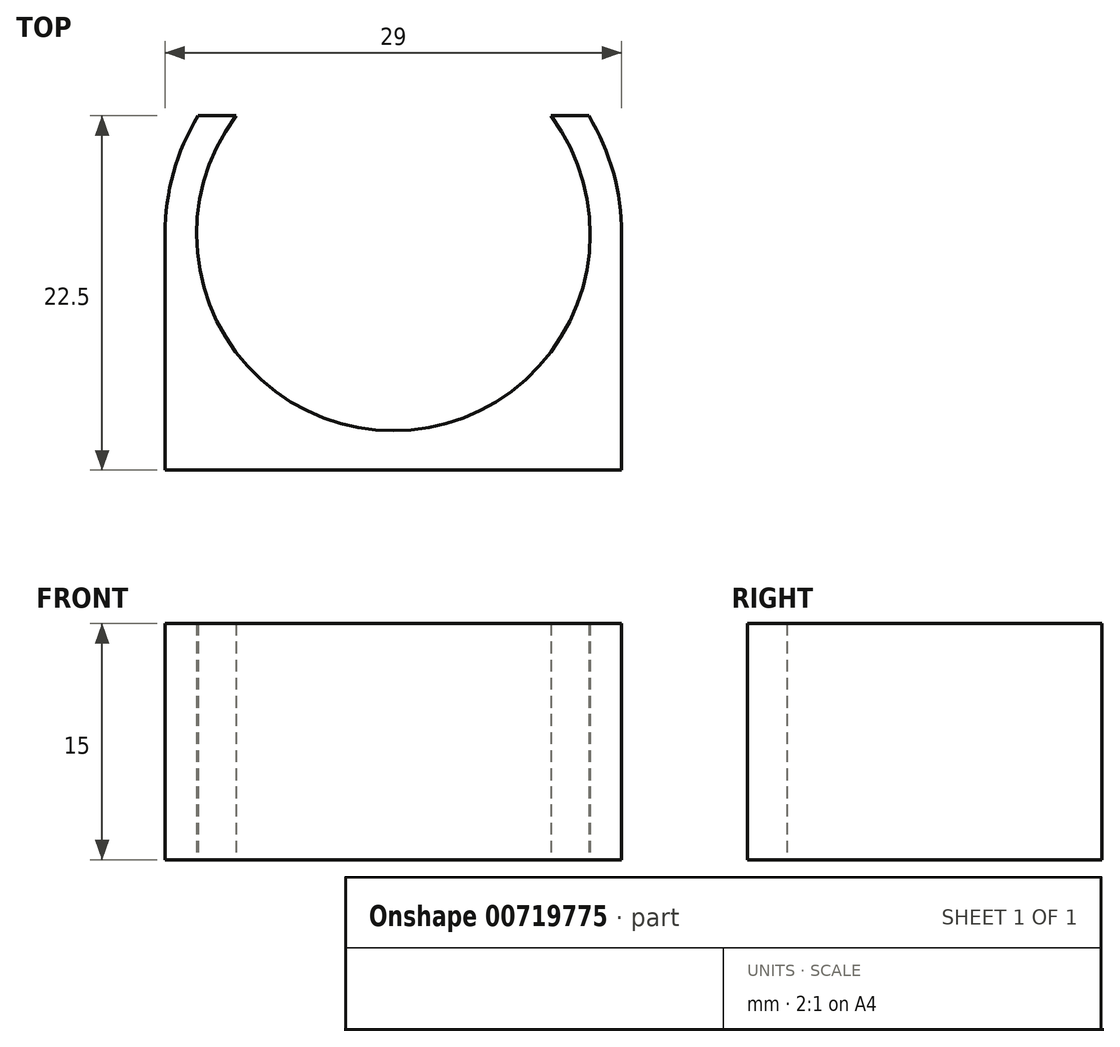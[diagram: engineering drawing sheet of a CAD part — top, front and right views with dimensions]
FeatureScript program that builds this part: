
annotation { "Feature Type Name" : "Feature", "Feature Type Description" : "" }
export const myFeature = defineFeature(function(context is Context, id is Id, definition is map)
    precondition{}
    {
        {
            var Q0;
            Q0=qCreatedBy(makeId("Top.planeOp"),FACE);
            var sketch = newSketch(context, id + "F0", { "sketchPlane" : qUnion([Q0])});
            skArc(sketch, "E0", {"start": v(4.5, 22.5) * mm, "mid": v(14.5, 2.5) * mm, "end": v(24.5, 22.5) * mm});
            skArc(sketch, "E1", {"start": v(2.1, 22.5) * mm, "mid": v(0.53, 18.9) * mm, "end": v(0, 15) * mm});
            skLineSegment(sketch, "E2", {"start": v(0, 15) * mm, "end": v(0, 0) * mm});
            skLineSegment(sketch, "E3", {"start": v(2.1, 22.5) * mm, "end": v(26.9, 22.5) * mm});
            skLineSegment(sketch, "E4", {"start": v(29, 15) * mm, "end": v(29, 0) * mm});
            skLineSegment(sketch, "E5", {"start": v(29, 0) * mm, "end": v(0, 0) * mm});
            skArc(sketch, "E6.trimOffspring", {"start": v(29, 15) * mm, "mid": v(28.47, 18.9) * mm, "end": v(26.9, 22.5) * mm});
            skSolve(sketch);
        }
        {
            var Q0;
            {var subQ1=sQuery(id+"F0.wireOp",EDGE,"E0");Q0=makeQuery(id+"F0.imprint","IMPRINT",FACE,{"disambiguationData":[TD([[makeQuery(id+"F0.imprint","IMPRINT",EDGE,{"derivedFrom":subQ1}),-1.0]])]});}
            extrude(context, id + "F1", {"entities" : qUnion([Q0]), "depth" : 15 * mm, "offsetDistance" : 25 * mm});
        }
    });
